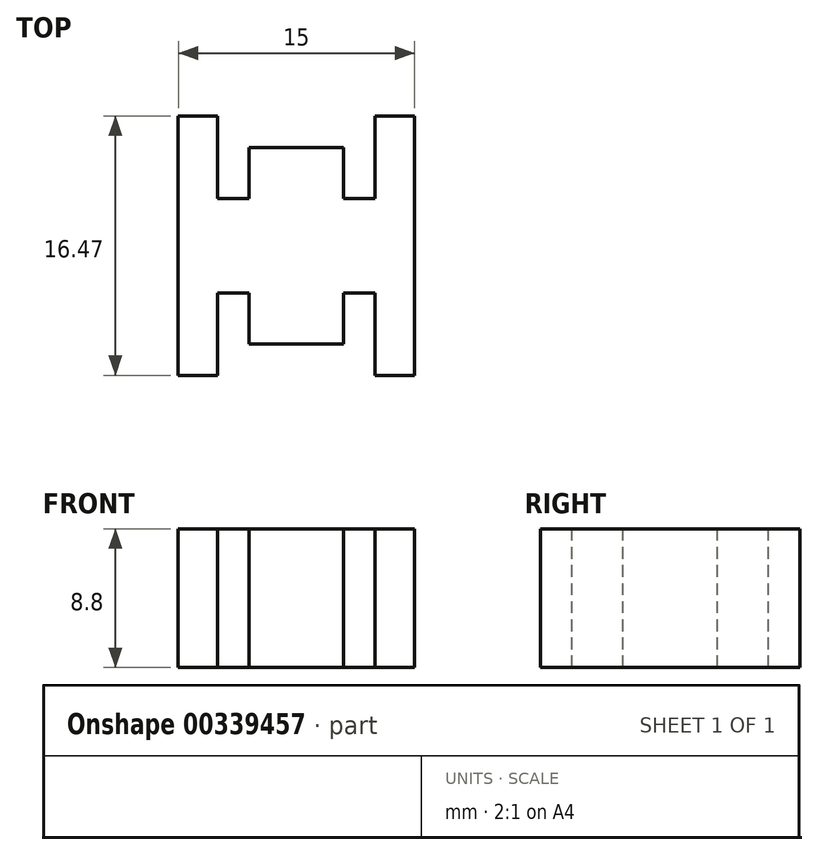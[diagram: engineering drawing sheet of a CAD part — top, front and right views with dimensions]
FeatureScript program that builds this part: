
annotation { "Feature Type Name" : "Feature", "Feature Type Description" : "" }
export const myFeature = defineFeature(function(context is Context, id is Id, definition is map)
    precondition{}
    {
        {
            var Q0;
            Q0=qCreatedBy(makeId("Top.planeOp"),FACE);
            var sketch = newSketch(context, id + "F0", { "sketchPlane" : qUnion([Q0])});
            skLineSegment(sketch, "E0.bottom", {"start": v(-23.1, 24.55) * mm, "end": v(-8.1, 24.55) * mm});
            skLineSegment(sketch, "E0.top", {"start": v(-23.1, 8.08) * mm, "end": v(-8.1, 8.08) * mm});
            skLineSegment(sketch, "E0.left", {"start": v(-23.1, 24.55) * mm, "end": v(-23.1, 8.08) * mm});
            skLineSegment(sketch, "E0.right", {"start": v(-8.1, 24.55) * mm, "end": v(-8.1, 8.08) * mm});
            skSolve(sketch);
        }
        {
            var Q0;
            Q0=qSketchRegion(id+"F0",true);
            extrude(context, id + "F1", {"entities" : qUnion([Q0]), "depth" : 8.8 * mm});
        }
        {
            var Q0;
            Q0=makeQuery(id+"F1.opExtrude","CAP_FACE",FACE,{"disambiguationData":[OSD([sQuery(id+"F0.wireOp",EDGE,"E0.bottom"),sQuery(id+"F0.wireOp",EDGE,"E0.top"),sQuery(id+"F0.wireOp",EDGE,"E0.left"),sQuery(id+"F0.wireOp",EDGE,"E0.right")])],"isStart":false});
            var sketch = newSketch(context, id + "F2", { "sketchPlane" : qUnion([Q0])});
            skLineSegment(sketch, "E1.bottom", {"start": v(-20.6, 8.08) * mm, "end": v(-10.6, 8.08) * mm});
            skLineSegment(sketch, "E1.top", {"start": v(-20.6, 13.32) * mm, "end": v(-10.6, 13.32) * mm});
            skLineSegment(sketch, "E1.left", {"start": v(-20.6, 8.08) * mm, "end": v(-20.6, 13.32) * mm});
            skLineSegment(sketch, "E1.right", {"start": v(-10.6, 8.08) * mm, "end": v(-10.6, 13.32) * mm});
            skLineSegment(sketch, "E2.bottom", {"start": v(-18.6, 13.32) * mm, "end": v(-12.6, 13.32) * mm});
            skLineSegment(sketch, "E2.top", {"start": v(-18.6, 10.08) * mm, "end": v(-12.6, 10.08) * mm});
            skLineSegment(sketch, "E2.left", {"start": v(-18.6, 13.32) * mm, "end": v(-18.6, 10.08) * mm});
            skLineSegment(sketch, "E2.right", {"start": v(-12.6, 13.32) * mm, "end": v(-12.6, 10.08) * mm});
            skLineSegment(sketch, "E3", {"start": v(-23.1, 16.32) * mm, "end": v(-8.1, 16.32) * mm, "construction": true});
            skLineSegment(sketch, "E4.MirrorCS", {"start": v(-20.6, 19.32) * mm, "end": v(-10.6, 19.32) * mm});
            skLineSegment(sketch, "E5.MirrorCS", {"start": v(-18.6, 19.32) * mm, "end": v(-18.6, 22.55) * mm});
            skLineSegment(sketch, "E6.MirrorCS", {"start": v(-18.6, 22.55) * mm, "end": v(-12.6, 22.55) * mm});
            skLineSegment(sketch, "E7.MirrorCS", {"start": v(-12.6, 19.32) * mm, "end": v(-12.6, 22.55) * mm});
            skLineSegment(sketch, "E8.MirrorCS", {"start": v(-10.6, 24.55) * mm, "end": v(-10.6, 19.32) * mm});
            skLineSegment(sketch, "E9.MirrorCS", {"start": v(-20.6, 24.55) * mm, "end": v(-20.6, 19.32) * mm});
            skLineSegment(sketch, "E10.MirrorCS", {"start": v(-20.6, 24.55) * mm, "end": v(-10.6, 24.55) * mm});
            skSolve(sketch);
        }
        {
            var Q0;
            Q0=makeQuery(id+"F2.imprint","IMPRINT",FACE,{"disambiguationData":[TD([[makeQuery(id+"F2.imprint","IMPRINT",EDGE,{"derivedFrom":sQuery(id+"F2.wireOp",EDGE,"E1.bottom")}),1.0]])]});
            var Q1;
            {var subQ0=sQuery(id+"F2.wireOp",EDGE,"E5.MirrorCS");Q1=makeQuery(id+"F2.imprint","IMPRINT",FACE,{"disambiguationData":[TD([[makeQuery(id+"F2.imprint","IMPRINT",EDGE,{"derivedFrom":subQ0}),1.0]])]});}
            extrude(context, id + "F3", {"entities" : qUnion([Q0, Q1]), "operationType" : NewBodyOperationType.REMOVE, "oppositeDirection" : true, "depth" : 25 * mm});
        }
    });
